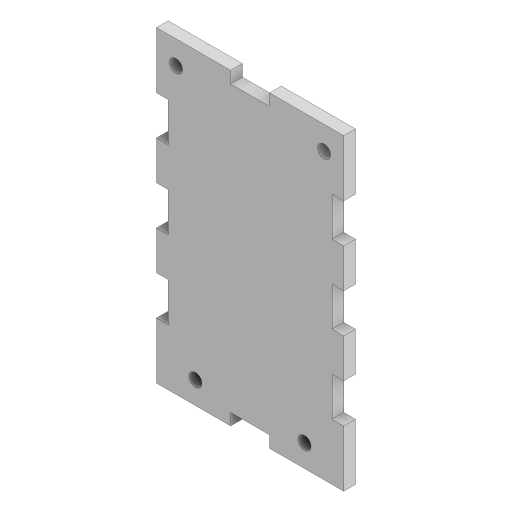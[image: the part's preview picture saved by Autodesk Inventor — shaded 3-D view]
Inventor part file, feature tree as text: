
AUTODESK INVENTOR PART (.ipt)
format: ipt  version: 2023.3 (Build 273359000, 359)  size: 163,328 bytes
history: native  units: mm
features: extrude x1, sketch x1
ambient origin geometry x8: Origin, YZ Plane, XZ Plane, XY Plane, X Axis, Y Axis, Z Axis, Center Point
bodies: Solid1 (feature_tree)
feature tree (2):
  extrude  "Extrusion1"  Depth=3.0mm TaperAngle=0.0deg
  sketch  "Sketch1"  dims[d1=20.0mm d3=10.0mm d5=20.0mm d7=10.0mm d9=20.0mm d11=10.0mm d13=20.0mm d15=10.0mm d16=3.3mm d17=3.3mm d18=28.0mm d19=14.0mm d20=3.3mm d21=3.3mm d22=38.0mm d23=19.0mm d24=34.0mm d25=44.0mm d26=3.25mm d27=20.0mm d28=5.0mm d29=10.0mm d30=9.0mm d31=26.0mm d32=7.0mm d33=1.0mm d34=3.0mm d35=10.0mm d36=10.0mm d37=3.0mm d38=10.0mm d39=3.0mm d40=20.0mm d41=20.0mm d42=3.0mm d43=10.0mm d44=20.0mm d45=20.0mm d46=10.0mm d47=10.0mm d48=10.0mm d49=10.0mm d50=3.0mm d51=0.0mm]
